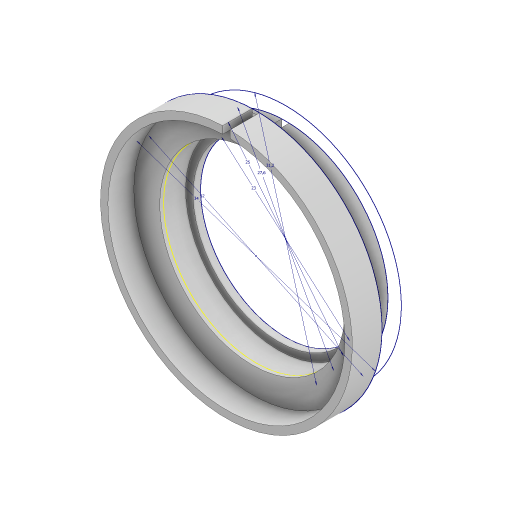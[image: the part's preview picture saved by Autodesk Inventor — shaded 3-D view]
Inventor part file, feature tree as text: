
AUTODESK INVENTOR PART (.ipt)
format: ipt  version: 2024 (Build 280153000, 153)  size: 199,680 bytes
history: native  units: mm
features: extrude x6, sketch x1
ambient origin geometry x8: Origin, YZ Plane, XZ Plane, XY Plane, X Axis, Y Axis, Z Axis, Center Point
bodies: Solid1 (feature_tree)
feature tree (7):
  extrude  "Extrusion1"  Depth=10.0mm
  extrude  "Extrusion2"  Depth=10.0mm
  extrude  "Extrusion3"  Depth=10.0mm
  extrude  "Extrusion5"  Depth=1.0mm TaperAngle=0.0deg
  extrude  "Extrusion6"  Depth=3.0mm TaperAngle=0.0deg
  extrude  "Extrusion10"  Depth=1.0mm TaperAngle=0.0deg
  sketch  "Sketch8"  dims[d0=27.6mm d1=23.0mm d2=31.2mm d3=25.0mm d4=1.0mm d5=0.0mm d6=3.0mm d7=0.0mm d8=1.0mm d9=0.0mm d14=32.0mm d15=34.0mm d16=0.5mm d17=0.0mm d18=4.0mm d19=0.0mm d30=1.0mm d31=10.0mm d32=10.0mm d33=0.0mm]
